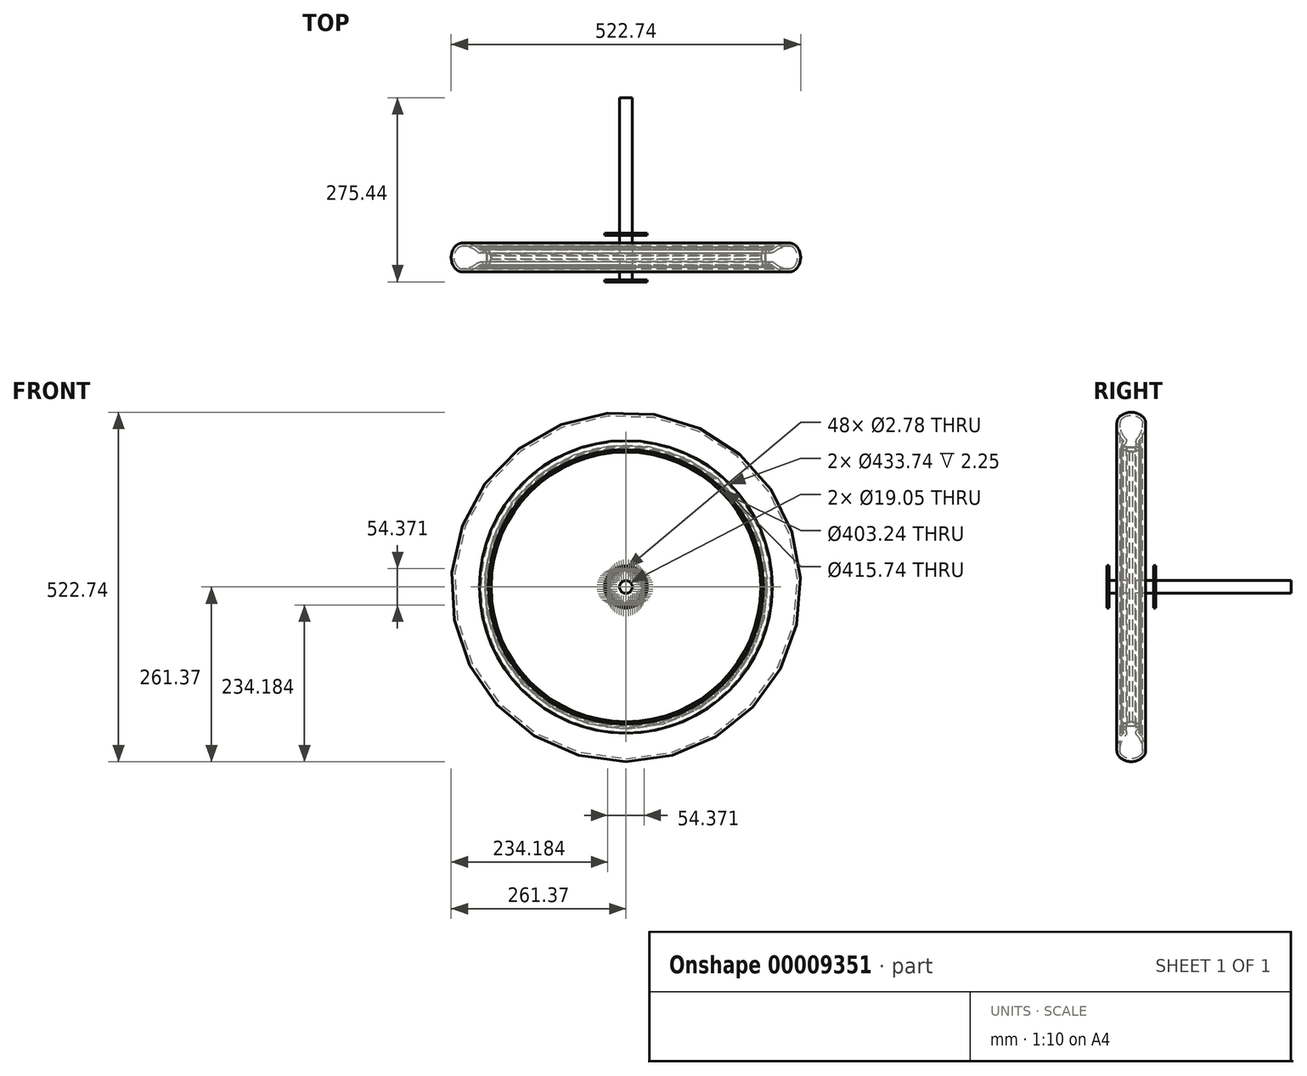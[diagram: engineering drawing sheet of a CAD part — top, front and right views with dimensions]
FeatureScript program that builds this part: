
annotation { "Feature Type Name" : "Feature", "Feature Type Description" : "" }
export const myFeature = defineFeature(function(context is Context, id is Id, definition is map)
    precondition{}
    {
        {
            var Q0;
            Q0=qCreatedBy(makeId("Front.planeOp"),FACE);
            var sketch = newSketch(context, id + "F0", { "sketchPlane" : qUnion([Q0])});
            skCircle(sketch, "E0", {"center": v(0, 0) * mm, "radius": 31.75 * mm});
            skCircle(sketch, "E1", {"center": v(0, 0) * mm, "radius": 9.53 * mm});
            skSolve(sketch);
        }
        {
            var Q0;
            Q0 = qSketchRegion(id + "F0", true);
            extrude(context, id + "F1", {"entities" : qUnion([Q0]), "depth" : 3.17 * mm});
        }
        {
            var Q0;
            Q0=qCreatedBy(makeId("Right.planeOp"),FACE);
            var sketch = newSketch(context, id + "F2", { "sketchPlane" : qUnion([Q0])});
            skLineSegment(sketch, "E2", {"start": v(-31.75, 0) * mm, "end": v(31.75, 0) * mm, "construction": true});
            skLineSegment(sketch, "E3", {"start": v(-31.75, 27.19) * mm, "end": v(31.75, 27.19) * mm, "construction": true});
            skPoint(sketch, "E4", {"position": v(-3.18, 28.57) * mm});
            skLineSegment(sketch, "E5", {"start": v(-3.18, 31.75) * mm, "end": v(0, 31.75) * mm, "construction": true});
            skSolve(sketch);
        }
        {
            var Q0;
            Q0=qCreatedBy(makeId("Right.planeOp"),FACE);
            var sketch = newSketch(context, id + "F3", { "sketchPlane" : qUnion([Q0])});
            skLineSegment(sketch, "E6", {"start": v(-3.18, 27.19) * mm, "end": v(-3.18, 29.37) * mm});
            skLineSegment(sketch, "E7", {"start": v(-3.18, 29.37) * mm, "end": v(-2.7, 28.57) * mm});
            skLineSegment(sketch, "E8", {"start": v(-2.7, 28.57) * mm, "end": v(-0.48, 28.57) * mm});
            skLineSegment(sketch, "E9", {"start": v(-0.48, 28.57) * mm, "end": v(0, 29.37) * mm});
            skLineSegment(sketch, "E10", {"start": v(0, 29.37) * mm, "end": v(0, 27.19) * mm});
            skLineSegment(sketch, "E11", {"start": v(0, 27.19) * mm, "end": v(-3.18, 27.19) * mm});
            skLineSegment(sketch, "E12", {"start": v(-1.59, 27.19) * mm, "end": v(-1.59, 31.75) * mm, "construction": true});
            skSolve(sketch);
        }
        {
            var Q0;
            Q0 = qSketchRegion(id + "F3", true);
            var Q1;
            Q1=sQuery(id+"F2.wireOp",EDGE,"E3");
            revolve(context, id + "F4", {"entities" : qUnion([Q0]), "axis" : qUnion([Q1]), "revolveType" : RevolveType.FULL, "oppositeDirection" : true});
        }
        {
            var Q0;
            Q0=makeQuery(id+"F4.opRevolve","SWEPT_BODY",BODY,{"disambiguationData":[OSD([sQuery(id+"F3.wireOp",EDGE,"E6"),sQuery(id+"F3.wireOp",EDGE,"E7"),sQuery(id+"F3.wireOp",EDGE,"E8"),sQuery(id+"F3.wireOp",EDGE,"E9"),sQuery(id+"F3.wireOp",EDGE,"E10"),sQuery(id+"F3.wireOp",EDGE,"E11")])]});
            var Q1;
            Q1=sQuery(id+"F2.wireOp",EDGE,"E2");
            circularPattern(context, id + "F5", {"operationType" : NewBodyOperationType.REMOVE, "entities" : qUnion([Q0]), "axis" : qUnion([Q1]), "angle" : 360 * degree, "instanceCount" : 24, "equalSpace" : true});
        }
        {
            var Q0;
            Q0=makeQuery(id+"F1.opExtrude","SWEPT_BODY",BODY,{"disambiguationData":[OSD([sQuery(id+"F0.wireOp",EDGE,"E0"),sQuery(id+"F0.wireOp",EDGE,"E1")])]});
            var Q1;
            Q1=sQuery(id+"F2.wireOp",EDGE,"E2");
            transform(context, id + "F6", {"entities" : qUnion([Q0]), "transformType" : TransformType.TRANSLATION_DISTANCE, "transformDirection" : qUnion([Q1]), "distance" : 69.85 * mm, "makeCopy" : true});
        }
        {
            var Q0;
            Q0=makeQuery(id+"F6.opPattern","COPY",BODY,{"derivedFrom":makeQuery(id+"F1.opExtrude","SWEPT_BODY",BODY,{"disambiguationData":[OSD([sQuery(id+"F0.wireOp",EDGE,"E0"),sQuery(id+"F0.wireOp",EDGE,"E1")])]}),"instanceName":"1"});
            var Q1;
            Q1=sQuery(id+"F2.wireOp",EDGE,"E2");
            transform(context, id + "F7", {"entities" : qUnion([Q0]), "transformType" : TransformType.ROTATION, "transformAxis" : qUnion([Q1]), "angle" : 7.5 * degree, "makeCopy" : false});
        }
        {
            var Q0;
            Q0=qCreatedBy(makeId("Right.planeOp"),FACE);
            var sketch = newSketch(context, id + "F8", { "sketchPlane" : qUnion([Q0])});
            skLineSegment(sketch, "E13", {"start": v(0, 0) * mm, "end": v(66.68, 0) * mm, "construction": true});
            skLineSegment(sketch, "E14", {"start": v(33.34, 0) * mm, "end": v(33.34, 218.87) * mm, "construction": true});
            skSolve(sketch);
        }
        {
            var Q0;
            Q0=qCreatedBy(makeId("Front.planeOp"),FACE);
            var Q1;
            Q1=sQuery(id+"F8.wireOp",VERTEX,"E14.start");
            cPlane(context, id + "F9", {"entities" : qUnion([Q0, Q1]), "cplaneType" : CPlaneType.PLANE_POINT, "offset" : 150 * mm, "width" : 150 * mm, "height" : 150 * mm});
        }
        {
            var Q0;
            Q0=qCreatedBy(id+"F9.planeOp",FACE);
            var sketch = newSketch(context, id + "F10", { "sketchPlane" : qUnion([Q0])});
            skCircle(sketch, "E15", {"center": v(0, 0) * mm, "radius": 218.87 * mm, "construction": true});
            skSolve(sketch);
        }
        {
            var Q0;
            Q0=qCreatedBy(makeId("Right.planeOp"),FACE);
            var sketch = newSketch(context, id + "F11", { "sketchPlane" : qUnion([Q0])});
            skLineSegment(sketch, "E16", {"start": v(33.34, 201.62) * mm, "end": v(30.84, 201.62) * mm});
            skLineSegment(sketch, "E17", {"start": v(18.34, 218.87) * mm, "end": v(21.59, 218.87) * mm});
            skLineSegment(sketch, "E18", {"start": v(18.34, 218.87) * mm, "end": v(18.34, 205.53) * mm});
            skLineSegment(sketch, "E19", {"start": v(18.34, 205.53) * mm, "end": v(30.84, 201.62) * mm});
            skLineSegment(sketch, "E20", {"start": v(21.59, 218.87) * mm, "end": v(21.59, 216.87) * mm});
            skLineSegment(sketch, "E21", {"start": v(21.59, 216.87) * mm, "end": v(19.34, 216.87) * mm});
            skLineSegment(sketch, "E22", {"start": v(19.34, 216.87) * mm, "end": v(19.34, 211.37) * mm});
            skLineSegment(sketch, "E23", {"start": v(19.34, 211.37) * mm, "end": v(27.34, 208.87) * mm});
            skLineSegment(sketch, "E24", {"start": v(27.34, 208.87) * mm, "end": v(33.34, 208.87) * mm});
            skLineSegment(sketch, "E25", {"start": v(33.34, 207.87) * mm, "end": v(27.18, 207.87) * mm});
            skLineSegment(sketch, "E26", {"start": v(27.18, 207.87) * mm, "end": v(19.34, 210.32) * mm});
            skLineSegment(sketch, "E27", {"start": v(19.34, 210.32) * mm, "end": v(19.34, 206.26) * mm});
            skLineSegment(sketch, "E28", {"start": v(19.34, 206.26) * mm, "end": v(31, 202.62) * mm});
            skLineSegment(sketch, "E29", {"start": v(31, 202.62) * mm, "end": v(33.34, 202.62) * mm});
            skLineSegment(sketch, "E30", {"start": v(19.34, 214.12) * mm, "end": v(18.34, 214.12) * mm, "construction": true});
            skLineSegment(sketch, "E31", {"start": v(23.34, 210.12) * mm, "end": v(23.04, 209.17) * mm, "construction": true});
            skLineSegment(sketch, "E32", {"start": v(25.16, 204.44) * mm, "end": v(24.87, 203.49) * mm, "construction": true});
            skLineSegment(sketch, "E33", {"start": v(30.34, 208.87) * mm, "end": v(30.34, 207.87) * mm, "construction": true});
            skLineSegment(sketch, "E34", {"start": v(32.16, 202.62) * mm, "end": v(32.16, 201.62) * mm, "construction": true});
            skLineSegment(sketch, "E35", {"start": v(33.34, 218.87) * mm, "end": v(33.34, 208.87) * mm, "construction": true});
            skLineSegment(sketch, "E36.0.MirrorCS", {"start": v(39.34, 208.87) * mm, "end": v(33.34, 208.87) * mm});
            skLineSegment(sketch, "E37.0.MirrorCS", {"start": v(47.34, 211.37) * mm, "end": v(39.34, 208.87) * mm});
            skLineSegment(sketch, "E38.0.MirrorCS", {"start": v(47.34, 216.87) * mm, "end": v(47.34, 211.37) * mm});
            skLineSegment(sketch, "E39.0.MirrorCS", {"start": v(45.09, 216.87) * mm, "end": v(47.34, 216.87) * mm});
            skLineSegment(sketch, "E40.0.MirrorCS", {"start": v(45.09, 218.87) * mm, "end": v(45.09, 216.87) * mm});
            skLineSegment(sketch, "E41.0.MirrorCS", {"start": v(48.34, 218.87) * mm, "end": v(45.09, 218.87) * mm});
            skLineSegment(sketch, "E42.0.MirrorCS", {"start": v(48.34, 218.87) * mm, "end": v(48.34, 205.53) * mm});
            skLineSegment(sketch, "E43.0.MirrorCS", {"start": v(48.34, 205.53) * mm, "end": v(35.84, 201.62) * mm});
            skLineSegment(sketch, "E44.0.MirrorCS", {"start": v(33.34, 201.62) * mm, "end": v(35.84, 201.62) * mm});
            skLineSegment(sketch, "E45.0.MirrorCS", {"start": v(35.68, 202.62) * mm, "end": v(33.34, 202.62) * mm});
            skLineSegment(sketch, "E46.0.MirrorCS", {"start": v(47.34, 206.26) * mm, "end": v(35.68, 202.62) * mm});
            skLineSegment(sketch, "E47.0.MirrorCS", {"start": v(47.34, 210.32) * mm, "end": v(47.34, 206.26) * mm});
            skLineSegment(sketch, "E48.0.MirrorCS", {"start": v(39.5, 207.87) * mm, "end": v(47.34, 210.32) * mm});
            skLineSegment(sketch, "E49.0.MirrorCS", {"start": v(33.34, 207.87) * mm, "end": v(39.5, 207.87) * mm});
            skSolve(sketch);
        }
        {
            var Q0;
            Q0 = qSketchRegion(id + "F11", true);
            var Q1;
            Q1=sQuery(id+"F8.wireOp",EDGE,"E13");
            revolve(context, id + "F12", {"entities" : qUnion([Q0]), "axis" : qUnion([Q1]), "revolveType" : RevolveType.FULL});
        }
        {
            var Q0;
            Q0=qCreatedBy(makeId("Right.planeOp"),FACE);
            var sketch = newSketch(context, id + "F13", { "sketchPlane" : qUnion([Q0])});
            skArc(sketch, "E50", {"start": v(21, 216.8) * mm, "mid": v(19.41, 214.05) * mm, "end": v(22.16, 212.46) * mm});
            skArc(sketch, "E51", {"start": v(21, 216.8) * mm, "mid": v(21.88, 217.64) * mm, "end": v(21.63, 218.83) * mm});
            skLineSegment(sketch, "E52", {"start": v(18.34, 261.37) * mm, "end": v(48.34, 261.37) * mm, "construction": true});
            skLineSegment(sketch, "E53", {"start": v(11.84, 261.37) * mm, "end": v(11.84, 218.87) * mm, "construction": true});
            skLineSegment(sketch, "E54", {"start": v(11.84, 244.87) * mm, "end": v(33.34, 244.87) * mm, "construction": true});
            skArc(sketch, "E55", {"start": v(11.84, 244.87) * mm, "mid": v(14.37, 230.96) * mm, "end": v(21.63, 218.83) * mm});
            skArc(sketch, "E56", {"start": v(33.34, 261.37) * mm, "mid": v(23.72, 259.45) * mm, "end": v(15.59, 253.98) * mm});
            skArc(sketch, "E57", {"start": v(15.59, 253.98) * mm, "mid": v(12.81, 249.8) * mm, "end": v(11.84, 244.87) * mm});
            skArc(sketch, "E58.0", {"start": v(22.16, 212.46) * mm, "mid": v(26.18, 216.33) * mm, "end": v(25, 221.79) * mm});
            skArc(sketch, "E58.1", {"start": v(16.33, 244.87) * mm, "mid": v(18.57, 232.54) * mm, "end": v(25, 221.79) * mm});
            skArc(sketch, "E58.2", {"start": v(18.77, 250.81) * mm, "mid": v(16.96, 248.09) * mm, "end": v(16.33, 244.87) * mm});
            skArc(sketch, "E58.3", {"start": v(33.34, 256.88) * mm, "mid": v(25.45, 255.3) * mm, "end": v(18.77, 250.81) * mm});
            skLineSegment(sketch, "E59", {"start": v(33.34, 261.37) * mm, "end": v(33.34, 218.87) * mm, "construction": true});
            skArc(sketch, "E60.0.MirrorCS", {"start": v(33.34, 261.37) * mm, "mid": v(42.95, 259.45) * mm, "end": v(51.09, 253.98) * mm});
            skArc(sketch, "E61.0.MirrorCS", {"start": v(51.09, 253.98) * mm, "mid": v(53.86, 249.8) * mm, "end": v(54.84, 244.87) * mm});
            skArc(sketch, "E62.0.MirrorCS", {"start": v(54.84, 244.87) * mm, "mid": v(52.3, 230.96) * mm, "end": v(45.05, 218.83) * mm});
            skArc(sketch, "E63.0.MirrorCS", {"start": v(45.67, 216.8) * mm, "mid": v(44.8, 217.64) * mm, "end": v(45.05, 218.83) * mm});
            skArc(sketch, "E64.0.MirrorCS", {"start": v(45.67, 216.8) * mm, "mid": v(47.26, 214.05) * mm, "end": v(44.52, 212.46) * mm});
            skArc(sketch, "E65.0.MirrorCS", {"start": v(44.52, 212.46) * mm, "mid": v(40.5, 216.33) * mm, "end": v(41.67, 221.79) * mm});
            skArc(sketch, "E66.0.MirrorCS", {"start": v(50.35, 244.87) * mm, "mid": v(48.1, 232.54) * mm, "end": v(41.67, 221.79) * mm});
            skArc(sketch, "E67.0.MirrorCS", {"start": v(47.9, 250.81) * mm, "mid": v(49.71, 248.09) * mm, "end": v(50.35, 244.87) * mm});
            skArc(sketch, "E68.0.MirrorCS", {"start": v(33.34, 256.88) * mm, "mid": v(41.23, 255.3) * mm, "end": v(47.9, 250.81) * mm});
            skSolve(sketch);
        }
        {
            var Q0;
            Q0 = qSketchRegion(id + "F13", true);
            var Q1;
            Q1=sQuery(id+"F8.wireOp",EDGE,"E13");
            revolve(context, id + "F14", {"entities" : qUnion([Q0]), "axis" : qUnion([Q1]), "revolveType" : RevolveType.FULL});
        }
        {
            var Q0;
            Q0=makeQuery(id+"F1.opExtrude","CAP_FACE",FACE,{"disambiguationData":[OSD([sQuery(id+"F0.wireOp",EDGE,"E0"),sQuery(id+"F0.wireOp",EDGE,"E1")])],"isStart":false});
            var sketch = newSketch(context, id + "F15", { "sketchPlane" : qUnion([Q0])});
            skCircle(sketch, "E69", {"center": v(0, 0) * mm, "radius": 9.53 * mm});
            skSolve(sketch);
        }
        {
            var Q0;
            Q0 = qSketchRegion(id + "F15", true);
            extrude(context, id + "F16", {"entities" : qUnion([Q0]), "oppositeDirection" : true, "depth" : 275.43 * mm});
        }
    });
